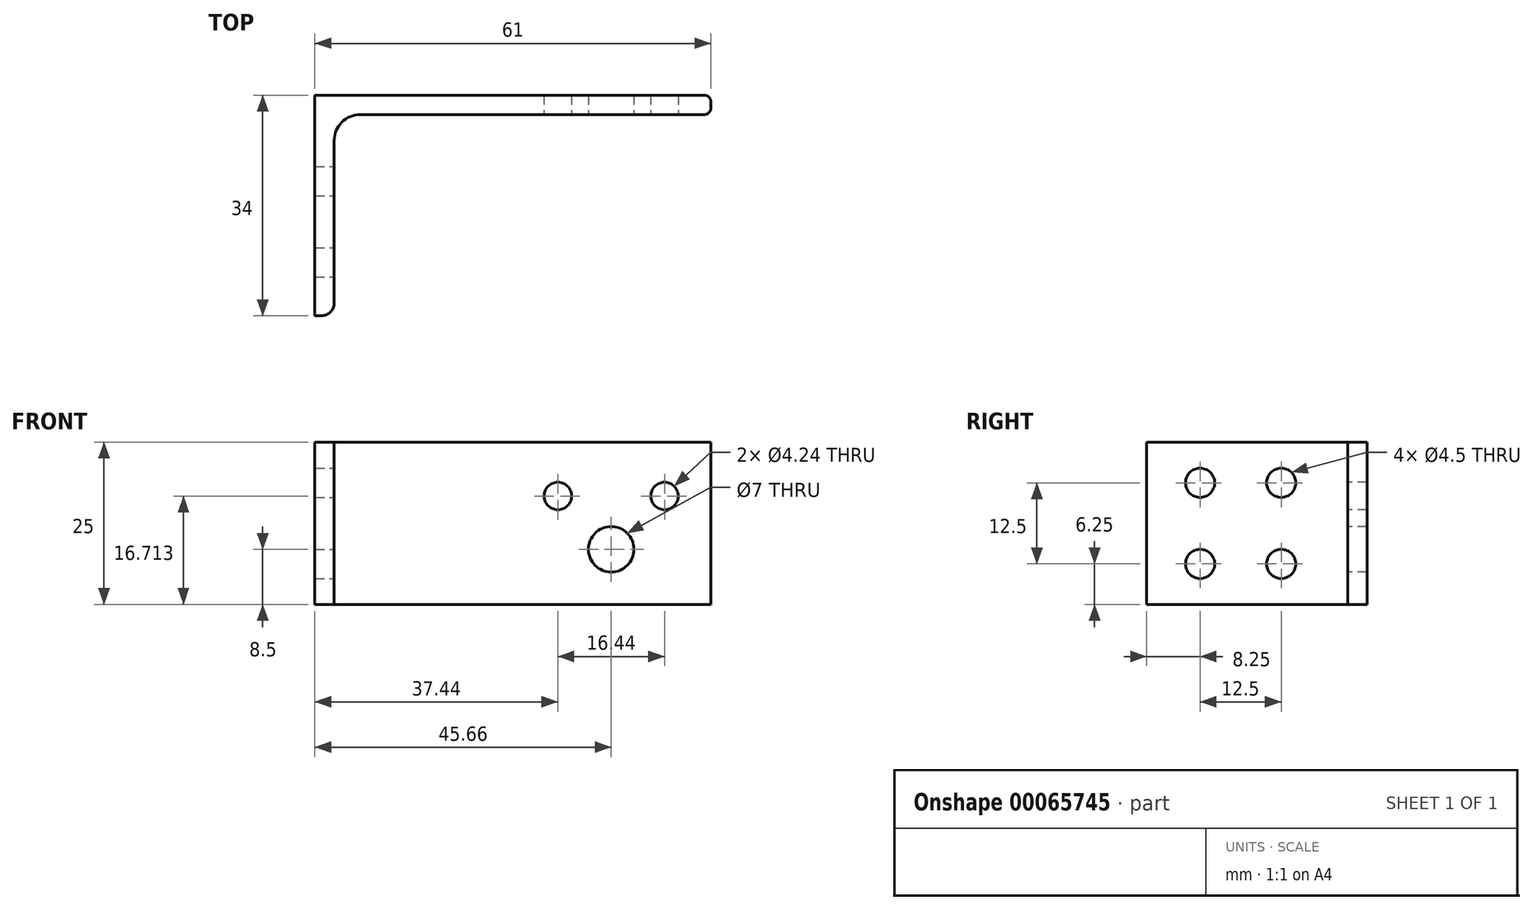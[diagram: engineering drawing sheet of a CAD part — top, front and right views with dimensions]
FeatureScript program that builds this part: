
annotation { "Feature Type Name" : "Feature", "Feature Type Description" : "" }
export const myFeature = defineFeature(function(context is Context, id is Id, definition is map)
    precondition{}
    {
        {
            var Q0;
            Q0=qCreatedBy(makeId("Top.planeOp"),FACE);
            var sketch = newSketch(context, id + "F0", { "sketchPlane" : qUnion([Q0])});
            skLineSegment(sketch, "E0", {"start": v(0, -29) * mm, "end": v(0, -4) * mm});
            skLineSegment(sketch, "E1", {"start": v(4, 0) * mm, "end": v(57, 0) * mm});
            skLineSegment(sketch, "E2", {"start": v(58, 1) * mm, "end": v(58, 2) * mm});
            skLineSegment(sketch, "E3", {"start": v(57, 3) * mm, "end": v(-3, 3) * mm});
            skLineSegment(sketch, "E4", {"start": v(-3, 3) * mm, "end": v(-3, -31) * mm});
            skLineSegment(sketch, "E5", {"start": v(-3, -31) * mm, "end": v(-2, -31) * mm});
            skPoint(sketch, "E6.visualSharp", {"position": v(0, -31) * mm});
            skArc(sketch, "E6.filletArc", {"start": v(-2, -31) * mm, "mid": v(-0.59, -30.41) * mm, "end": v(0, -29) * mm});
            skPoint(sketch, "E7.visualSharp", {"position": v(58, 0) * mm});
            skArc(sketch, "E7.filletArc", {"start": v(57, 0) * mm, "mid": v(57.7, 0.3) * mm, "end": v(58, 1) * mm});
            skPoint(sketch, "E8.visualSharp", {"position": v(58, 3) * mm});
            skArc(sketch, "E8.filletArc", {"start": v(58, 2) * mm, "mid": v(57.7, 2.7) * mm, "end": v(57, 3) * mm});
            skLineSegment(sketch, "E9", {"start": v(-3, -15.76) * mm, "end": v(0, -15.76) * mm, "construction": true});
            skLineSegment(sketch, "E10", {"start": v(18.75, 0) * mm, "end": v(18.75, 3) * mm, "construction": true});
            skPoint(sketch, "E11.visualSharp", {"position": v(0, 0) * mm});
            skArc(sketch, "E11.filletArc", {"start": v(4, 0) * mm, "mid": v(1.17, -1.17) * mm, "end": v(0, -4) * mm});
            skSolve(sketch);
        }
        {
            var Q0;
            Q0=makeQuery(id+"F0.imprint","IMPRINT",FACE,{"disambiguationData":[TD([[makeQuery(id+"F0.imprint","IMPRINT",EDGE,{"derivedFrom":sQuery(id+"F0.wireOp",EDGE,"E0")}),1.0]])]});
            extrude(context, id + "F1", {"entities" : qUnion([Q0]), "depth" : 25 * mm});
        }
        {
            var Q0;
            Q0=makeQuery(id+"F1.opExtrude","SWEPT_FACE",FACE,{"disambiguationData":[OSD([sQuery(id+"F0.wireOp",EDGE,"E0")])]});
            var sketch = newSketch(context, id + "F2", { "sketchPlane" : qUnion([Q0])});
            skCircle(sketch, "E12", {"center": v(-22.75, 6.25) * mm, "radius": 2.25 * mm});
            skCircle(sketch, "E13", {"center": v(-10.25, 6.25) * mm, "radius": 2.25 * mm});
            skCircle(sketch, "E14", {"center": v(-22.75, 18.75) * mm, "radius": 2.25 * mm});
            skCircle(sketch, "E15", {"center": v(-10.25, 18.75) * mm, "radius": 2.25 * mm});
            skLineSegment(sketch, "E16", {"start": v(-16.5, 0) * mm, "end": v(-16.5, 25) * mm, "construction": true});
            skLineSegment(sketch, "E17", {"start": v(-29, 12.5) * mm, "end": v(-16.5, 12.5) * mm, "construction": true});
            skLineSegment(sketch, "E18", {"start": v(-16.5, 12.5) * mm, "end": v(-4, 12.5) * mm, "construction": true});
            skPoint(sketch, "E19", {"position": v(-10.25, 12.5) * mm});
            skLineSegment(sketch, "E20", {"start": v(-28.1, 12.5) * mm, "end": v(-28.1, 25) * mm, "construction": true});
            skPoint(sketch, "E21", {"position": v(-28.1, 18.75) * mm});
            skSolve(sketch);
        }
        {
            var Q0;
            Q0=makeQuery(id+"F2.imprint","IMPRINT",FACE,{"disambiguationData":[TD([[makeQuery(id+"F2.imprint","IMPRINT",EDGE,{"derivedFrom":sQuery(id+"F2.wireOp",EDGE,"E14")}),1.0]])]});
            var Q1;
            Q1=makeQuery(id+"F2.imprint","IMPRINT",FACE,{"disambiguationData":[TD([[makeQuery(id+"F2.imprint","IMPRINT",EDGE,{"derivedFrom":sQuery(id+"F2.wireOp",EDGE,"E15")}),1.0]])]});
            var Q2;
            Q2=makeQuery(id+"F2.imprint","IMPRINT",FACE,{"disambiguationData":[TD([[makeQuery(id+"F2.imprint","IMPRINT",EDGE,{"derivedFrom":sQuery(id+"F2.wireOp",EDGE,"E13")}),1.0]])]});
            var Q3;
            Q3=makeQuery(id+"F2.imprint","IMPRINT",FACE,{"disambiguationData":[TD([[makeQuery(id+"F2.imprint","IMPRINT",EDGE,{"derivedFrom":sQuery(id+"F2.wireOp",EDGE,"E12")}),1.0]])]});
            extrude(context, id + "F3", {"entities" : qUnion([Q0, Q1, Q2, Q3]), "operationType" : NewBodyOperationType.REMOVE, "oppositeDirection" : true, "depth" : 25 * mm});
        }
        {
            var Q0;
            Q0=makeQuery(id+"F1.opExtrude","SWEPT_FACE",FACE,{"disambiguationData":[OSD([sQuery(id+"F0.wireOp",EDGE,"E1")])]});
            var sketch = newSketch(context, id + "F4", { "sketchPlane" : qUnion([Q0])});
            skCircle(sketch, "E22", {"center": v(34.44, 16.71) * mm, "radius": 2.12 * mm});
            skCircle(sketch, "E23", {"center": v(42.66, 8.5) * mm, "radius": 3.5 * mm});
            skCircle(sketch, "E24", {"center": v(50.88, 16.71) * mm, "radius": 2.12 * mm});
            skSolve(sketch);
        }
        {
            var Q0;
            Q0=makeQuery(id+"F4.imprint","IMPRINT",FACE,{"disambiguationData":[TD([[makeQuery(id+"F4.imprint","IMPRINT",EDGE,{"derivedFrom":sQuery(id+"F4.wireOp",EDGE,"E23")}),1.0]])]});
            var Q1;
            Q1=makeQuery(id+"F4.imprint","IMPRINT",FACE,{"disambiguationData":[TD([[makeQuery(id+"F4.imprint","IMPRINT",EDGE,{"derivedFrom":sQuery(id+"F4.wireOp",EDGE,"E24")}),1.0]])]});
            var Q2;
            Q2=makeQuery(id+"F4.imprint","IMPRINT",FACE,{"disambiguationData":[TD([[makeQuery(id+"F4.imprint","IMPRINT",EDGE,{"derivedFrom":sQuery(id+"F4.wireOp",EDGE,"E22")}),1.0]])]});
            extrude(context, id + "F5", {"entities" : qUnion([Q0, Q1, Q2]), "operationType" : NewBodyOperationType.REMOVE, "oppositeDirection" : true, "depth" : 25 * mm});
        }
    });
